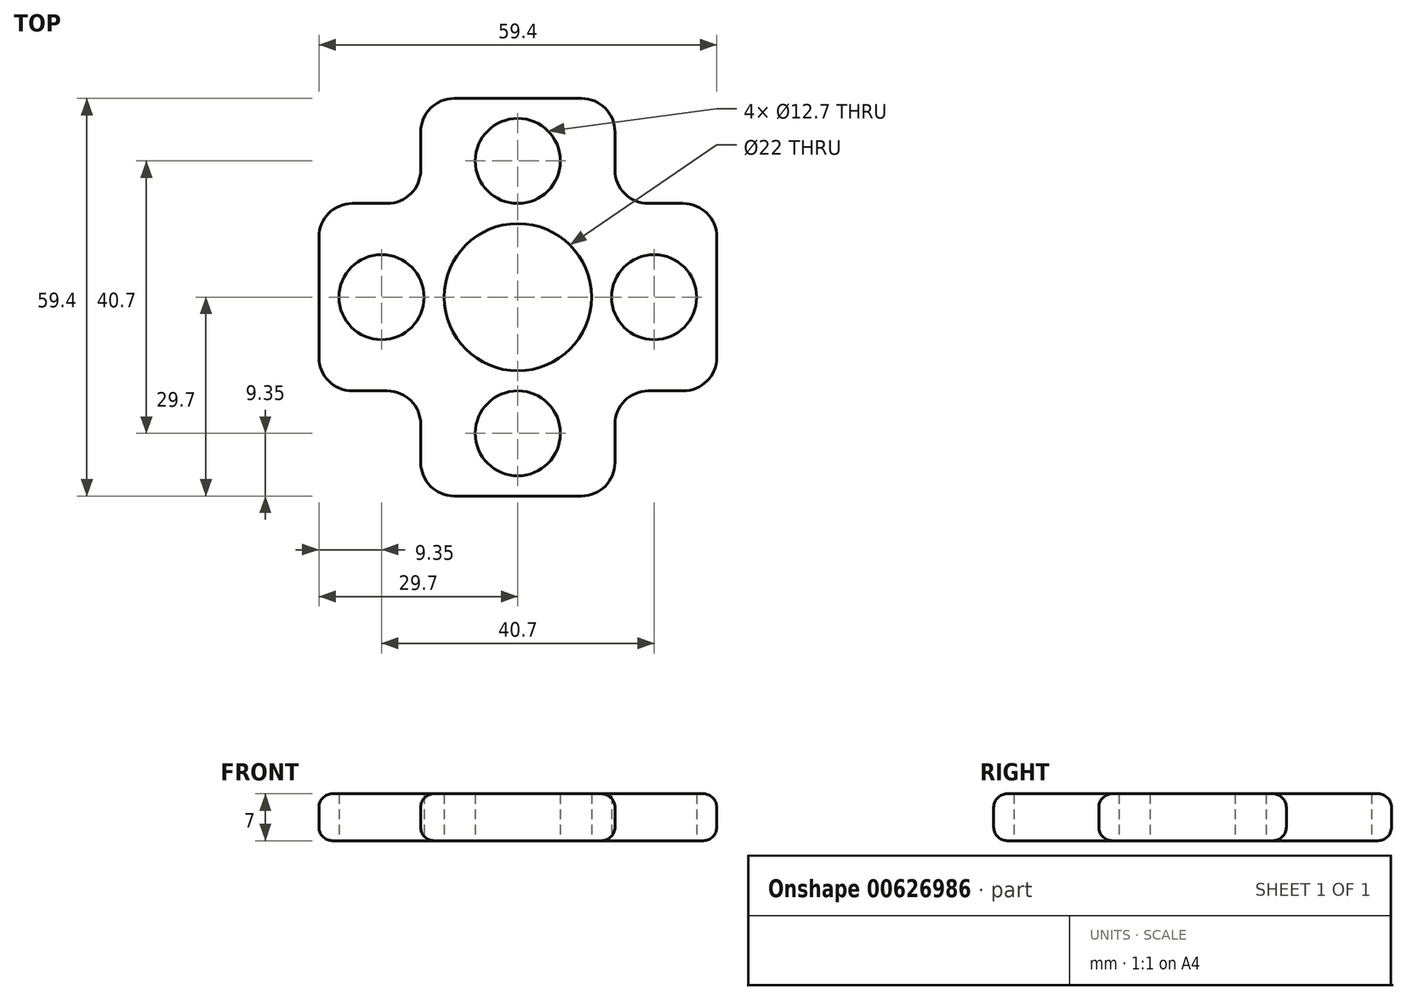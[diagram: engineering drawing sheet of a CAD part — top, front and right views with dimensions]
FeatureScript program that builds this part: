
annotation { "Feature Type Name" : "Feature", "Feature Type Description" : "" }
export const myFeature = defineFeature(function(context is Context, id is Id, definition is map)
    precondition{}
    {
        {
            var Q0;
            Q0=qCreatedBy(makeId("Top.planeOp"),FACE);
            var sketch = newSketch(context, id + "F0", { "sketchPlane" : qUnion([Q0])});
            skLineSegment(sketch, "E0.bottom", {"start": v(-29.7, 14) * mm, "end": v(-14.5, 14) * mm});
            skLineSegment(sketch, "E0.top", {"start": v(-29.7, -14) * mm, "end": v(-14.5, -14) * mm});
            skLineSegment(sketch, "E0.left", {"start": v(-29.7, 14) * mm, "end": v(-29.7, -14) * mm});
            skLineSegment(sketch, "E0.right", {"start": v(29.7, 14) * mm, "end": v(29.7, -14) * mm});
            skPoint(sketch, "E0.middle", {"position": v(0, 0) * mm});
            skLineSegment(sketch, "E1.bottom", {"start": v(14.5, 29.7) * mm, "end": v(-14.5, 29.7) * mm});
            skLineSegment(sketch, "E1.top", {"start": v(14.5, -29.7) * mm, "end": v(-14.5, -29.7) * mm});
            skLineSegment(sketch, "E1.left", {"start": v(14.5, 29.7) * mm, "end": v(14.5, 14) * mm});
            skLineSegment(sketch, "E1.right", {"start": v(-14.5, 29.7) * mm, "end": v(-14.5, 14) * mm});
            skLineSegment(sketch, "E2.trimOffspring", {"start": v(14.5, 14) * mm, "end": v(29.7, 14) * mm});
            skLineSegment(sketch, "E3.trimOffspring", {"start": v(14.5, -14) * mm, "end": v(29.7, -14) * mm});
            skLineSegment(sketch, "E4.trimOffspring", {"start": v(-14.5, -14) * mm, "end": v(-14.5, -29.7) * mm});
            skLineSegment(sketch, "E5.trimOffspring", {"start": v(14.5, -14) * mm, "end": v(14.5, -29.7) * mm});
            skSolve(sketch);
        }
        {
            var Q0;
            Q0=makeQuery(id+"F0.imprint","IMPRINT",FACE,{"disambiguationData":[TD([[makeQuery(id+"F0.imprint","IMPRINT",EDGE,{"derivedFrom":sQuery(id+"F0.wireOp",EDGE,"E0.bottom")}),-1.0]])]});
            extrude(context, id + "F1", {"entities" : qUnion([Q0]), "depth" : 7 * mm, "offsetDistance" : 25 * mm});
        }
        {
            var Q0;
            Q0=qCreatedBy(makeId("Top.planeOp"),FACE);
            var sketch = newSketch(context, id + "F2", { "sketchPlane" : qUnion([Q0])});
            skCircle(sketch, "E6", {"center": v(0, 0) * mm, "radius": 11 * mm});
            skSolve(sketch);
        }
        {
            var Q0;
            Q0 = qSketchRegion(id + "F2", true);
            extrude(context, id + "F3", {"entities" : qUnion([Q0]), "operationType" : NewBodyOperationType.REMOVE, "depth" : 47.4 * mm, "offsetDistance" : 25 * mm});
        }
        {
            var Q0;
            Q0=qCreatedBy(makeId("Top.planeOp"),FACE);
            var sketch = newSketch(context, id + "F4", { "sketchPlane" : qUnion([Q0])});
            skCircle(sketch, "E7", {"center": v(-20.35, 0) * mm, "radius": 6.35 * mm});
            skLineSegment(sketch, "E8", {"start": v(-14, 30.3) * mm, "end": v(-14, -30.14) * mm, "construction": true});
            skCircle(sketch, "E9.MirrorC", {"center": v(20.35, 0) * mm, "radius": 6.35 * mm});
            skCircle(sketch, "E10", {"center": v(0, 0) * mm, "radius": 20.35 * mm, "construction": true});
            skCircle(sketch, "E11", {"center": v(0, 20.35) * mm, "radius": 6.35 * mm});
            skCircle(sketch, "E12.MirrorC", {"center": v(0, -20.35) * mm, "radius": 6.35 * mm});
            skSolve(sketch);
        }
        {
            var Q0;
            Q0 = qSketchRegion(id + "F4", true);
            extrude(context, id + "F5", {"entities" : qUnion([Q0]), "operationType" : NewBodyOperationType.REMOVE, "endBound" : BoundingType.SYMMETRIC, "depth" : 25 * mm, "offsetDistance" : 25 * mm});
        }
        {
            var Q0;
            Q0=makeQuery(id+"F1.opExtrude","SWEPT_EDGE",EDGE,{"disambiguationData":[OSD([sQuery(id+"F0.wireOp",EDGE,"E3.trimOffspring"),sQuery(id+"F0.wireOp",EDGE,"E5.trimOffspring")])]});
            var Q1;
            Q1=makeQuery(id+"F1.opExtrude","SWEPT_EDGE",EDGE,{"disambiguationData":[OSD([sQuery(id+"F0.wireOp",EDGE,"E1.left"),sQuery(id+"F0.wireOp",EDGE,"E2.trimOffspring")])]});
            var Q2;
            Q2=makeQuery(id+"F1.opExtrude","SWEPT_EDGE",EDGE,{"disambiguationData":[OSD([sQuery(id+"F0.wireOp",EDGE,"E0.bottom"),sQuery(id+"F0.wireOp",EDGE,"E1.right")])]});
            var Q3;
            Q3=makeQuery(id+"F1.opExtrude","SWEPT_EDGE",EDGE,{"disambiguationData":[OSD([sQuery(id+"F0.wireOp",EDGE,"E0.top"),sQuery(id+"F0.wireOp",EDGE,"E4.trimOffspring")])]});
            fillet(context, id + "F6", {"entities" : qUnion([Q0, Q1, Q2, Q3]), "radius" : 5 * mm, "tangentPropagation" : true, "allowEdgeOverflow" : false});
        }
        {
            var Q0;
            Q0=makeQuery(id+"F1.opExtrude","SWEPT_EDGE",EDGE,{"disambiguationData":[OSD([sQuery(id+"F0.wireOp",EDGE,"E1.top"),sQuery(id+"F0.wireOp",EDGE,"E5.trimOffspring")])]});
            var Q1;
            Q1=makeQuery(id+"F1.opExtrude","SWEPT_EDGE",EDGE,{"disambiguationData":[OSD([sQuery(id+"F0.wireOp",EDGE,"E1.top"),sQuery(id+"F0.wireOp",EDGE,"E4.trimOffspring")])]});
            var Q2;
            Q2=makeQuery(id+"F1.opExtrude","SWEPT_EDGE",EDGE,{"disambiguationData":[OSD([sQuery(id+"F0.wireOp",EDGE,"E0.right"),sQuery(id+"F0.wireOp",EDGE,"E3.trimOffspring")])]});
            var Q3;
            Q3=makeQuery(id+"F1.opExtrude","SWEPT_EDGE",EDGE,{"disambiguationData":[OSD([sQuery(id+"F0.wireOp",EDGE,"E0.right"),sQuery(id+"F0.wireOp",EDGE,"E2.trimOffspring")])]});
            var Q4;
            Q4=makeQuery(id+"F1.opExtrude","SWEPT_EDGE",EDGE,{"disambiguationData":[OSD([sQuery(id+"F0.wireOp",EDGE,"E1.bottom"),sQuery(id+"F0.wireOp",EDGE,"E1.left")])]});
            var Q5;
            Q5=makeQuery(id+"F1.opExtrude","SWEPT_EDGE",EDGE,{"disambiguationData":[OSD([sQuery(id+"F0.wireOp",EDGE,"E1.bottom"),sQuery(id+"F0.wireOp",EDGE,"E1.right")])]});
            var Q6;
            Q6=makeQuery(id+"F1.opExtrude","SWEPT_EDGE",EDGE,{"disambiguationData":[OSD([sQuery(id+"F0.wireOp",EDGE,"E0.bottom"),sQuery(id+"F0.wireOp",EDGE,"E0.left")])]});
            var Q7;
            Q7=makeQuery(id+"F1.opExtrude","SWEPT_EDGE",EDGE,{"disambiguationData":[OSD([sQuery(id+"F0.wireOp",EDGE,"E0.top"),sQuery(id+"F0.wireOp",EDGE,"E0.left")])]});
            fillet(context, id + "F7", {"entities" : qUnion([Q0, Q1, Q2, Q3, Q4, Q5, Q6, Q7]), "radius" : 5 * mm, "tangentPropagation" : true, "allowEdgeOverflow" : false});
        }
        {
            var Q0;
            Q0=makeQuery(id+"F1.opExtrude","CAP_EDGE",EDGE,{"disambiguationData":[OSD([sQuery(id+"F0.wireOp",EDGE,"E1.top")])],"isStart":false});
            var Q1;
            Q1=makeQuery(id+"F1.opExtrude","CAP_EDGE",EDGE,{"disambiguationData":[OSD([sQuery(id+"F0.wireOp",EDGE,"E1.top")])],"isStart":true});
            fillet(context, id + "F8", {"entities" : qUnion([Q0, Q1]), "radius" : 2 * mm, "tangentPropagation" : true, "allowEdgeOverflow" : false});
        }
    });
